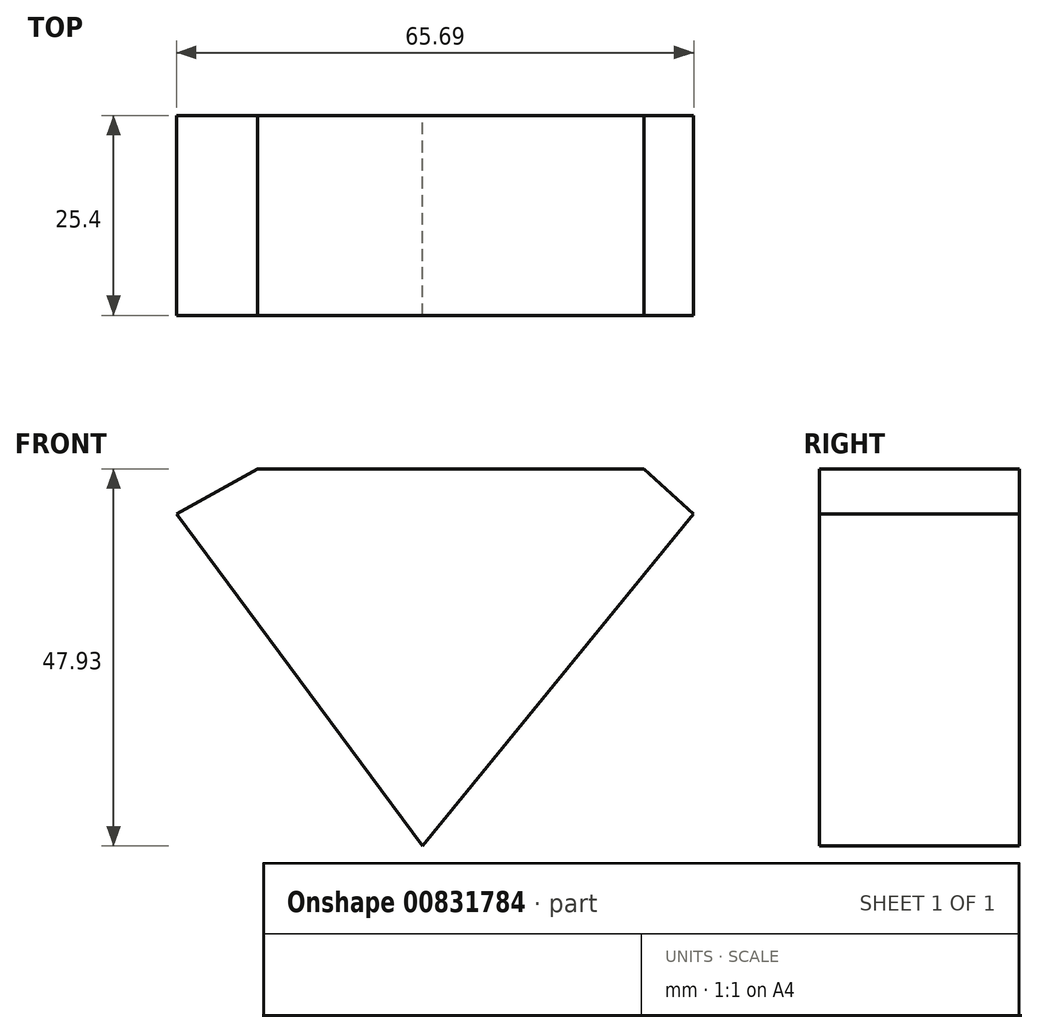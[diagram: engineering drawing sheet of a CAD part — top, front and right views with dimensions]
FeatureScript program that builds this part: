
annotation { "Feature Type Name" : "Feature", "Feature Type Description" : "" }
export const myFeature = defineFeature(function(context is Context, id is Id, definition is map)
    precondition{}
    {
        {
            var Q0;
            Q0=qCreatedBy(makeId("Front.planeOp"),FACE);
            var sketch = newSketch(context, id + "F0", { "sketchPlane" : qUnion([Q0])});
            skLineSegment(sketch, "E0", {"start": v(-20.9, 11.36) * mm, "end": v(28.17, 11.36) * mm});
            skLineSegment(sketch, "E1", {"start": v(28.17, 11.36) * mm, "end": v(34.47, 5.63) * mm});
            skLineSegment(sketch, "E2", {"start": v(34.47, 5.63) * mm, "end": v(0, -36.57) * mm});
            skLineSegment(sketch, "E3", {"start": v(0, -36.57) * mm, "end": v(-31.22, 5.63) * mm});
            skLineSegment(sketch, "E4", {"start": v(-31.22, 5.63) * mm, "end": v(-20.9, 11.36) * mm});
            skSolve(sketch);
        }
        {
            var Q0;
            Q0 = qSketchRegion(id + "F0", true);
            extrude(context, id + "F1", {"entities" : qUnion([Q0]), "depth" : 25.4 * mm, "offsetDistance" : 25.4 * mm});
        }
    });
